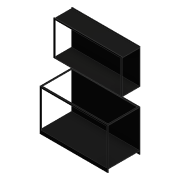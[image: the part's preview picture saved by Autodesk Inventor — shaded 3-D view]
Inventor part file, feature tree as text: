
AUTODESK INVENTOR PART (.ipt)
format: ipt  version: 2016 (Build 200138000, 138)  size: 251,904 bytes
history: native  units: mm
features: extrude x9, projected_geometry x9, sketch x8, plane x1
ambient origin geometry x8: Origin, YZ Plane, XZ Plane, XY Plane, X Axis, Y Axis, Z Axis, Center Point
bodies: Solid1 (feature_tree)
feature tree (27):
  extrude  "Extrusion1"  Depth=10.0mm
  extrude  "Extrusion2"  Depth=80.0mm
  extrude  "Extrusion3"  Depth=30.0mm
  extrude  "Extrusion4"  Depth=30.0mm
  plane  "Work Plane1"
  extrude  "Extrusion5"  Depth=10.0mm
  extrude  "Extrusion9"  Depth=10.0mm
  extrude  "Extrusión10"  Depth=30.0mm
  extrude  "Extrusión11"  TaperAngle=0.0deg  [1 undecoded]
  extrude  "Extrusion13"  Depth=1737.5mm
  sketch  "Sketch1"  dims[d3=0.0mm d5=10.0mm]
  sketch  "Sketch2"  dims[d6=10.0mm d7=80.0mm]
  projected_geometry  "Projected Loop1"
  sketch  "Sketch3"  dims[d9=0.0mm d10=30.0mm]
  projected_geometry  "Projected Loop2"
  sketch  "Sketch4"  dims[d11=400.0mm d12=0.0mm d13=30.0mm]
  projected_geometry  "Projected Loop3"
  projected_geometry  "Projected Loop4"
  projected_geometry  "Projected Loop5"
  sketch  "Sketch5"  dims[d14=30.0mm d15=10.0mm]
  sketch  "Sketch9"  dims[d16=0.0mm d18=10.0mm]
  projected_geometry  "Projected Loop9"
  sketch  "Boceto10"  dims[d19=0.0mm d32=30.0mm]
  projected_geometry  "Contorno proyectado10"
  projected_geometry  "Contorno proyectado11"
  sketch  "Sketch13"  dims[d33=10.0mm d34=0.0mm d36=1737.5mm d39=10.0mm d40=10.0mm d41=10.0mm d43=0.0mm d44=30.0mm d45=30.0mm d46=30.0mm d48=750.0mm d49=0.0mm d53=10.0mm d54=20.0mm d55=1737.5mm d56=0.0mm]
  projected_geometry  "Projected Loop12"
note: 1 required parameter value undecoded (feature->parameter linkage not recoverable at this tier; creation-order binding heuristic only, values carry confidence <= 0.55)
